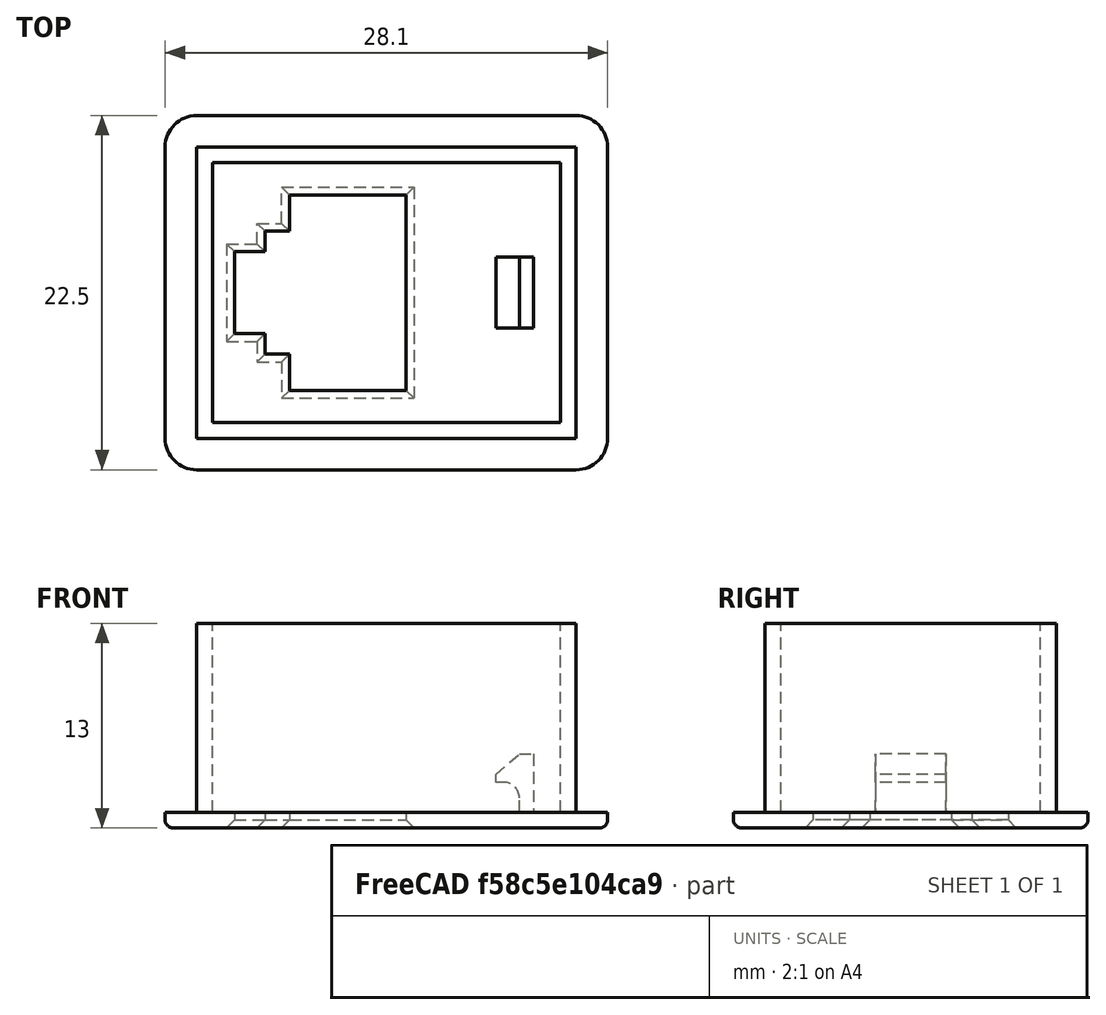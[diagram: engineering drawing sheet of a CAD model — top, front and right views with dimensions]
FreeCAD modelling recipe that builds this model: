
FCSTD DOCUMENT  (FreeCAD 0.17RUnknown)
Label: test116_lanport
License: All rights reserved
LicenseURL: http://en.wikipedia.org/wiki/All_rights_reserved
objects: Sketcher::SketchObject×5, PartDesign::Pad×3, PartDesign::Plane×2, PartDesign::Fillet×1, PartDesign::Chamfer×1, PartDesign::Body×1, Mesh::Feature×1
note: 16 computed .brp shape members not serialized (recipe doc carries the construction recipe); baked Part::Feature solids carry a one-line shape summary decoded from their .brp

FEATURE [Sketcher::SketchObject] Sketch  label="LanChanger"
  MapMode = 5
  Support = -> [XY_Plane]
  sketch-geometry (24):
    g0: LineSegment [constr] StartX=-5.25 StartY=6 StartZ=0 EndX=5.25 EndY=6 EndZ=0
    g1: LineSegment [constr] StartX=5.25 StartY=6 StartZ=0 EndX=5.25 EndY=-6 EndZ=0
    g2: LineSegment [constr] StartX=5.25 StartY=-6 StartZ=0 EndX=-5.25 EndY=-6 EndZ=0
    g3: LineSegment [constr] StartX=-5.25 StartY=-6 StartZ=0 EndX=-5.25 EndY=6 EndZ=0
    g4: LineSegment StartX=-1.75 StartY=6 StartZ=0 EndX=5.25 EndY=6 EndZ=0
    g5: LineSegment StartX=-1.75 StartY=6 StartZ=0 EndX=-1.75 EndY=3.7 EndZ=0
    g6: LineSegment StartX=-1.75 StartY=3.7 StartZ=0 EndX=-3.3 EndY=3.7 EndZ=0
    g7: LineSegment StartX=-3.3 StartY=3.7 StartZ=0 EndX=-3.3 EndY=2.4 EndZ=0
    g8: LineSegment StartX=-3.3 StartY=2.4 StartZ=0 EndX=-5.25 EndY=2.4 EndZ=0
    g9: LineSegment StartX=-1.75 StartY=-3.7 StartZ=0 EndX=-3.3 EndY=-3.7 EndZ=0
    g10: LineSegment StartX=-3.3 StartY=-3.7 StartZ=0 EndX=-3.3 EndY=-2.4 EndZ=0
    g11: LineSegment StartX=-3.3 StartY=-2.4 StartZ=0 EndX=-5.25 EndY=-2.4 EndZ=0
    g12: LineSegment StartX=-1.75 StartY=-6 StartZ=0 EndX=5.25 EndY=-6 EndZ=0
    g13: LineSegment StartX=-1.75 StartY=-6 StartZ=0 EndX=-1.75 EndY=-3.7 EndZ=0
    g14: LineSegment StartX=-5.25 StartY=-2.4 StartZ=0 EndX=-5.25 EndY=2.4 EndZ=0
    g15: LineSegment StartX=5.25 StartY=6 StartZ=0 EndX=5.25 EndY=-6 EndZ=0
    g16: LineSegment StartX=-6.65 StartY=8.05 StartZ=0 EndX=15.05 EndY=8.05 EndZ=0
    g17: LineSegment StartX=15.05 StartY=8.05 StartZ=0 EndX=15.05 EndY=-8.05 EndZ=0
    g18: LineSegment StartX=15.05 StartY=-8.05 StartZ=0 EndX=-6.65 EndY=-8.05 EndZ=0
    g19: LineSegment StartX=-6.65 StartY=-8.05 StartZ=0 EndX=-6.65 EndY=8.05 EndZ=0
    g20: LineSegment StartX=11.65 StartY=2.45 StartZ=0 EndX=13.75 EndY=2.45 EndZ=0
    g21: LineSegment StartX=13.75 StartY=2.45 StartZ=0 EndX=13.75 EndY=-2.45 EndZ=0
    g22: LineSegment StartX=13.75 StartY=-2.45 StartZ=0 EndX=11.65 EndY=-2.45 EndZ=0
    g23: LineSegment StartX=11.65 StartY=-2.45 StartZ=0 EndX=11.65 EndY=2.45 EndZ=0
  constraints (69):
    c: Coincident(g0,g1)
    c: Coincident(g1,g2)
    c: Coincident(g2,g3)
    c: Coincident(g3,g0)
    c: Horizontal(g0)
    c: Horizontal(g2)
    c: Vertical(g1)
    c: Vertical(g3)
    c: Symmetric(g0,g1,g-1)
    c: Distance(g1) = 12
    c: Distance(g0) = 10.5
    c: PointOnObject(g4,g0)
    c: Coincident(g4,g0)
    c: Distance(g4) = 7
    c: Coincident(g4,g5)
    c: Vertical(g5)
    c: Coincident(g5,g6)
    c: Horizontal(g6)
    c: Coincident(g6,g7)
    c: Vertical(g7)
    c: Coincident(g7,g8)
    c: PointOnObject(g8,g3)
    c: Horizontal(g8)
    c: Distance(g5) = 2.3
    c: Distance(g6) = 1.55
    c: Distance(g7) = 1.3
    c: Distance(g12) = 7
    c: Coincident(g12,g13)
    c: Vertical(g13)
    c: Coincident(g13,g9)
    c: Horizontal(g9)
    c: Coincident(g9,g10)
    c: Vertical(g10)
    c: Coincident(g10,g11)
    c: Horizontal(g11)
    c: Distance(g13) = 2.3
    c: Distance(g9) = 1.55
    c: Distance(g10) = 1.3
    c: Coincident(g14,g11)
    c: Coincident(g14,g8)
    c: Coincident(g15,g0)
    c: Coincident(g15,g1)
    c: Coincident(g12,g1)
    c: PointOnObject(g12,g2)
    c: PointOnObject(g14,g3)
    c: Coincident(g16,g17)
    c: Coincident(g17,g18)
    c: Coincident(g18,g19)
    c: Coincident(g19,g16)
    c: Horizontal(g16)
    c: Horizontal(g18)
    c: Vertical(g17)
    c: Vertical(g19)
    c: Symmetric(g16,g18,g-1)
    c: Distance(g16) = 21.7
    c: Distance(g8,g19) = 1.4
    c: Distance(g19) = 16.1
    c: Coincident(g20,g21)
    c: Coincident(g21,g22)
    c: Coincident(g22,g23)
    c: Coincident(g23,g20)
    c: Horizontal(g20)
    c: Horizontal(g22)
    c: Vertical(g21)
    c: Vertical(g23)
    c: Symmetric(g22,g20,g-1)
    c: Distance(g20,g17) = 1.3
    c: Distance(g20) = 2.1
    c: Distance(g21) = 4.9
FEATURE [Sketcher::SketchObject] Sketch001
  ExternalGeometry = -> [Sketch]
  MapMode = 5
  Support = -> [XY_Plane]
  sketch-geometry (8):
    g0: LineSegment StartX=-7.85 StartY=9.25 StartZ=0 EndX=16.25 EndY=9.25 EndZ=0
    g1: LineSegment StartX=16.25 StartY=9.25 StartZ=0 EndX=16.25 EndY=-9.25 EndZ=0
    g2: LineSegment StartX=16.25 StartY=-9.25 StartZ=0 EndX=-7.85 EndY=-9.25 EndZ=0
    g3: LineSegment StartX=-7.85 StartY=-9.25 StartZ=0 EndX=-7.85 EndY=9.25 EndZ=0
    g4: LineSegment StartX=-6.85 StartY=8.25 StartZ=0 EndX=15.25 EndY=8.25 EndZ=0
    g5: LineSegment StartX=15.25 StartY=8.25 StartZ=0 EndX=15.25 EndY=-8.25 EndZ=0
    g6: LineSegment StartX=15.25 StartY=-8.25 StartZ=0 EndX=-6.85 EndY=-8.25 EndZ=0
    g7: LineSegment StartX=-6.85 StartY=-8.25 StartZ=0 EndX=-6.85 EndY=8.25 EndZ=0
  constraints (24):
    c: Coincident(g0,g1)
    c: Coincident(g1,g2)
    c: Coincident(g2,g3)
    c: Coincident(g3,g0)
    c: Horizontal(g0)
    c: Horizontal(g2)
    c: Vertical(g1)
    c: Vertical(g3)
    c: Coincident(g4,g5)
    c: Coincident(g5,g6)
    c: Coincident(g6,g7)
    c: Coincident(g7,g4)
    c: Horizontal(g4)
    c: Horizontal(g6)
    c: Vertical(g5)
    c: Vertical(g7)
    c: Distance(g4,g1) = 1
    c: Symmetric(g4,g5,g-1)
    c: Distance(g-3,g4) = 0.2
    c: Distance(g-4,g7) = 0.2
    c: Distance(g-3,g5) = 0.2
    c: Distance(g4,g0) = 1
    c: Symmetric(g0,g1,g-1)
    c: Distance(g4,g3) = 1
FEATURE [PartDesign::Pad] Pad
  Length = 12
  Length2 = 100
  Profile = -> Sketch001
  Type = 0
FEATURE [Sketcher::SketchObject] Sketch002
  ExternalGeometry = -> [Pad,Sketch]
  MapMode = 5
  Placement = pos=(0,0,0) rot=(1,0,0;3.14159rad)
  Support = -> [Pad]
  sketch-geometry (20):
    g0: LineSegment StartX=-7.85 StartY=11.25 StartZ=0 EndX=16.25 EndY=11.25 EndZ=0
    g1: LineSegment StartX=18.25 StartY=9.25 StartZ=0 EndX=18.25 EndY=-9.25 EndZ=0
    g2: LineSegment StartX=16.25 StartY=-11.25 StartZ=0 EndX=-7.85 EndY=-11.25 EndZ=0
    g3: LineSegment StartX=-9.85 StartY=-9.25 StartZ=0 EndX=-9.85 EndY=9.25 EndZ=0
    g4: ArcOfCircle CenterX=-7.85 CenterY=9.25 CenterZ=0 NormalX=0 NormalY=0 NormalZ=1 AngleXU=0 Radius=2 StartAngle=1.5708 EndAngle=3.14159
    g5: ArcOfCircle CenterX=16.25 CenterY=9.25 CenterZ=0 NormalX=0 NormalY=0 NormalZ=1 AngleXU=0 Radius=2 StartAngle=0 EndAngle=1.5708
    g6: ArcOfCircle CenterX=16.25 CenterY=-9.25 CenterZ=0 NormalX=0 NormalY=0 NormalZ=1 AngleXU=0 Radius=2 StartAngle=4.71239 EndAngle=6.28319
    g7: ArcOfCircle CenterX=-7.85 CenterY=-9.25 CenterZ=0 NormalX=0 NormalY=0 NormalZ=1 AngleXU=0 Radius=2 StartAngle=3.14159 EndAngle=4.71239
    g8: LineSegment StartX=-5.45 StartY=2.6 StartZ=0 EndX=-3.5 EndY=2.6 EndZ=0
    g9: LineSegment StartX=-3.5 StartY=2.6 StartZ=0 EndX=-3.5 EndY=3.9 EndZ=0
    g10: LineSegment StartX=-3.5 StartY=3.9 StartZ=0 EndX=-1.95 EndY=3.9 EndZ=0
    g11: LineSegment StartX=-1.95 StartY=3.9 StartZ=0 EndX=-1.95 EndY=6.2 EndZ=0
    g12: LineSegment StartX=-1.95 StartY=6.2 StartZ=0 EndX=5.45 EndY=6.2 EndZ=0
    g13: LineSegment StartX=-5.45 StartY=-2.6 StartZ=0 EndX=-3.5 EndY=-2.6 EndZ=0
    g14: LineSegment StartX=-3.5 StartY=-2.6 StartZ=0 EndX=-3.5 EndY=-3.9 EndZ=0
    g15: LineSegment StartX=-3.5 StartY=-3.9 StartZ=0 EndX=-1.95 EndY=-3.9 EndZ=0
    g16: LineSegment StartX=-1.95 StartY=-3.9 StartZ=0 EndX=-1.95 EndY=-6.2 EndZ=0
    g17: LineSegment StartX=-1.95 StartY=-6.2 StartZ=0 EndX=5.45 EndY=-6.2 EndZ=0
    g18: LineSegment StartX=-5.45 StartY=-2.6 StartZ=0 EndX=-5.45 EndY=2.6 EndZ=0
    g19: LineSegment StartX=5.45 StartY=-6.2 StartZ=0 EndX=5.45 EndY=6.2 EndZ=0
  constraints (53):
    c: Horizontal(g0)
    c: Horizontal(g2)
    c: Vertical(g1)
    c: Vertical(g3)
    c: Tangent(g3,g4) = 1.5708
    c: Tangent(g0,g4) = 1.5708
    c: Tangent(g0,g5) = 1.5708
    c: Tangent(g1,g5) = 1.5708
    c: Tangent(g1,g6) = 1.5708
    c: Tangent(g2,g6) = 1.5708
    c: Tangent(g2,g7) = 1.5708
    c: Tangent(g3,g7) = 1.5708
    c: Radius(g4) = 2
    c: Equal(g4,g5)
    c: Equal(g4,g6)
    c: Equal(g4,g7)
    c: Coincident(g5,g-3)
    c: Coincident(g7,g-4)
    c: Horizontal(g8)
    c: Coincident(g8,g9)
    c: Vertical(g9)
    c: Coincident(g9,g10)
    c: Coincident(g10,g11)
    c: Coincident(g11,g12)
    c: Horizontal(g12)
    c: Vertical(g11)
    c: Horizontal(g10)
    c: Equal(g-6,g8)
    c: Equal(g10,g-5)
    c: Equal(g-8,g9)
    c: Equal(g-9,g11)
    c: DistanceX(g11,g-9) = 0.2
    c: DistanceY(g-9,g11) = 0.2
    c: Horizontal(g13)
    c: Coincident(g13,g14)
    c: Vertical(g14)
    c: Coincident(g14,g15)
    c: Coincident(g15,g16)
    c: Coincident(g16,g17)
    c: Horizontal(g17)
    c: Vertical(g16)
    c: Horizontal(g15)
    c: Equal(g-6,g13)
    c: Equal(g14,g-8)
    c: Equal(g-5,g15)
    c: Equal(g16,g-9)
    c: Coincident(g18,g13)
    c: Coincident(g18,g8)
    c: Symmetric(g8,g13,g-1)
    c: Coincident(g19,g17)
    c: Coincident(g19,g12)
    c: Vertical(g19)
    c: DistanceX(g-7,g12) = 0.2
FEATURE [PartDesign::Pad] Pad001
  BaseFeature = -> Pad
  Length = 1
  Length2 = 100
  Profile = -> Sketch002
  Type = 0
FEATURE [Sketcher::SketchObject] Sketch003
  ExternalGeometry = -> [Sketch]
  MapMode = 5
  Support = -> [Pad001]
  sketch-geometry (4):
    g0: LineSegment StartX=12.65 StartY=2.25 StartZ=0 EndX=13.55 EndY=2.25 EndZ=0
    g1: LineSegment StartX=13.55 StartY=2.25 StartZ=0 EndX=13.55 EndY=-2.25 EndZ=0
    g2: LineSegment StartX=13.55 StartY=-2.25 StartZ=0 EndX=12.65 EndY=-2.25 EndZ=0
    g3: LineSegment StartX=12.65 StartY=-2.25 StartZ=0 EndX=12.65 EndY=2.25 EndZ=0
  constraints (12):
    c: Coincident(g0,g1)
    c: Coincident(g1,g2)
    c: Coincident(g2,g3)
    c: Coincident(g3,g0)
    c: Horizontal(g0)
    c: Horizontal(g2)
    c: Vertical(g1)
    c: Vertical(g3)
    c: Symmetric(g0,g1,g-1)
    c: Distance(g1,g-6) = 0.2
    c: Distance(g0,g-3) = 0.2
    c: Distance(g2,g-4) = 1
FEATURE [PartDesign::Plane] DatumPlane
  MapMode = 1
  Placement = pos=(12.65,2.25,0) rot=(1,0,0;1.5708rad)
  Support = -> [Sketch003]
FEATURE [Sketcher::SketchObject] Sketch004
  ExternalGeometry = -> [Sketch,Sketch003]
  MapMode = 5
  Placement = pos=(12.65,2.25,0) rot=(0,0.707107,0.707107;3.14159rad)
  Support = -> [DatumPlane]
  sketch-geometry (9):
    g0: LineSegment StartX=-0.9 StartY=0 StartZ=0 EndX=0 EndY=0 EndZ=0
    g1: LineSegment StartX=0 StartY=0 StartZ=0 EndX=0 EndY=0.9 EndZ=0
    g2: LineSegment StartX=0.006483 StartY=3.7 StartZ=0 EndX=-0.9 EndY=3.7 EndZ=0
    g3: LineSegment StartX=-0.9 StartY=3.7 StartZ=0 EndX=-0.9 EndY=0 EndZ=0
    g4: LineSegment StartX=1 StartY=1.9 StartZ=0 EndX=1.5 EndY=1.9 EndZ=0
    g5: LineSegment StartX=1.5 StartY=1.9 StartZ=0 EndX=1.5 EndY=2.4 EndZ=0
    g6: LineSegment StartX=1.5 StartY=2.4 StartZ=0 EndX=0.006483 EndY=3.7 EndZ=0
    g7: LineSegment [constr] StartX=1 StartY=0 StartZ=0 EndX=1 EndY=3.22096 EndZ=0
    g8: ArcOfCircle CenterX=1 CenterY=0.9 CenterZ=0 NormalX=0 NormalY=0 NormalZ=1 AngleXU=0 Radius=1 StartAngle=1.5708 EndAngle=3.14159
  constraints (23):
    c: Coincident(g0,g1)
    c: Coincident(g2,g3)
    c: Coincident(g3,g0)
    c: Horizontal(g0)
    c: Horizontal(g2)
    c: Vertical(g1)
    c: Vertical(g3)
    c: Coincident(g0,g-5)
    c: Coincident(g-1,g0)
    c: Distance(g3) = 3.7
    c: Horizontal(g4)
    c: Coincident(g4,g5)
    c: Vertical(g5)
    c: Coincident(g5,g6)
    c: Coincident(g6,g2)
    c: Coincident(g7,g-3)
    c: Vertical(g7)
    c: Tangent(g1,g8) = 1.5708
    c: Tangent(g4,g8) = 1.5708
    c: Radius(g8) = 1
    c: Distance(g5,g7) = 0.5
    c: Equal(g4,g5)
    c: DistanceY(g7,g4) = 1.9
FEATURE [PartDesign::Plane] DatumPlane001
  MapMode = 7
  Placement = pos=(12.65,-2.25,0) rot=(1,0,0;1.5708rad)
  Support = -> [Sketch003]
FEATURE [PartDesign::Pad] Pad002
  BaseFeature = -> Pad001
  Length = 4.5
  Length2 = 100
  Profile = -> Sketch004
  Reversed = true
  Type = 3
  UpToFace = -> DatumPlane001 [Plane]
FEATURE [PartDesign::Fillet] Fillet
  Base = -> Pad002 [Edge57]
  BaseFeature = -> Pad002
  Radius = 0.5
FEATURE [PartDesign::Chamfer] Chamfer
  Base = -> Fillet [Edge38,Edge37,Edge36,Edge35,Edge34,Edge33,Edge44,Edge43,Edge42,Edge41,Edge40,Edge39]
  BaseFeature = -> Fillet
  Size = 0.5
FEATURE [PartDesign::Body] Body
  Group = -> [Sketch,Sketch001,Pad,Sketch002,Pad001,Sketch003,DatumPlane,Sketch004,Pad002,DatumPlane001,Fillet,Chamfer]
  Origin = -> Origin
  Tip = -> Chamfer
FEATURE [Mesh::Feature] Mesh  label="Chamfer (Meshed)"
